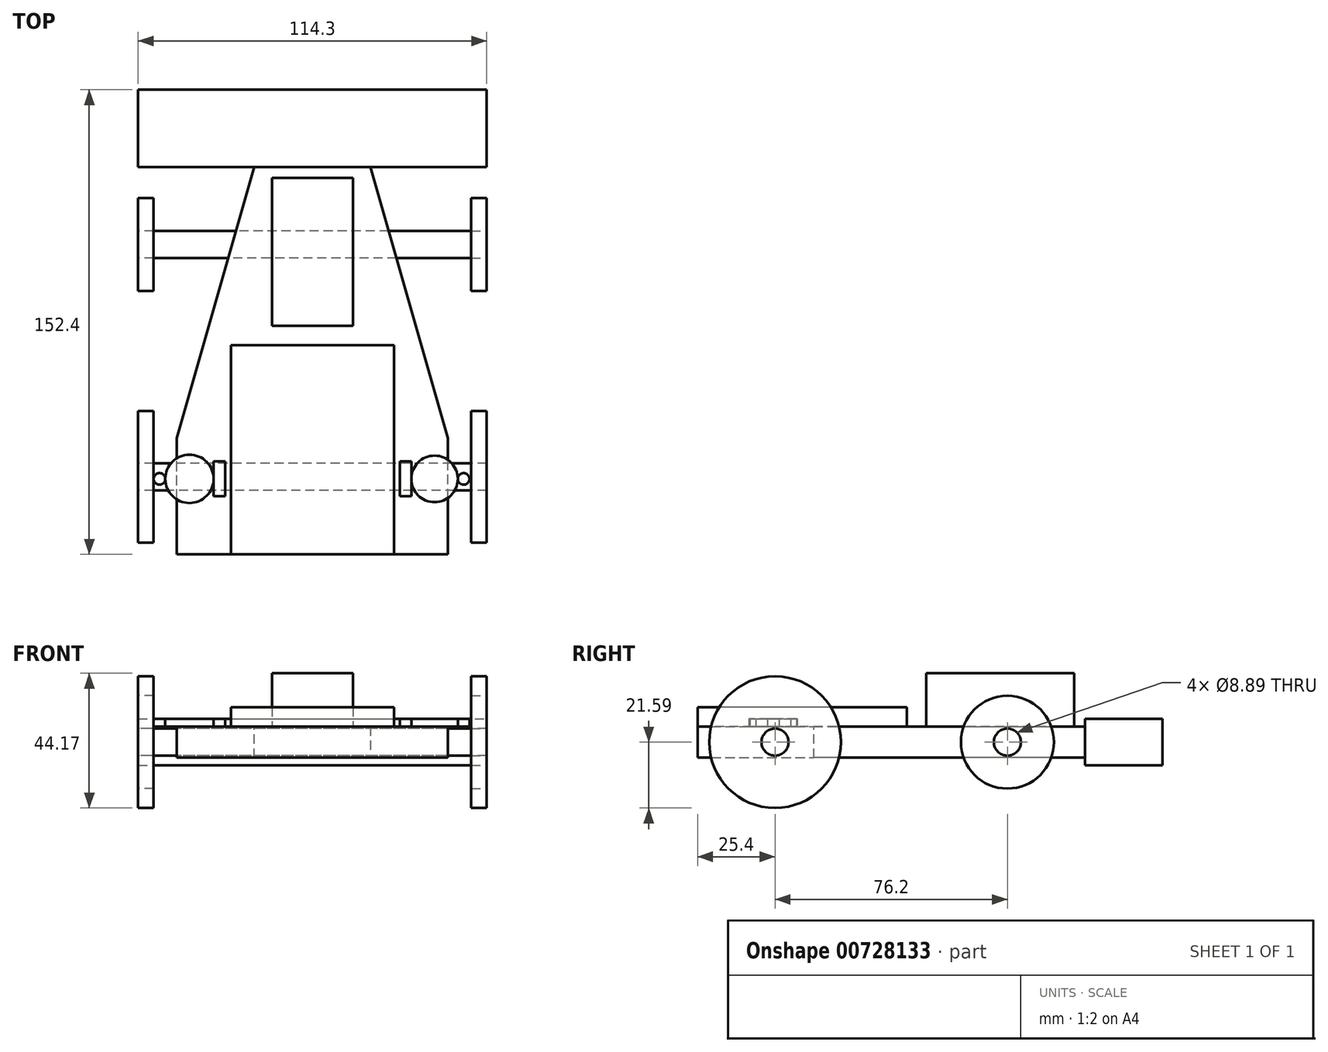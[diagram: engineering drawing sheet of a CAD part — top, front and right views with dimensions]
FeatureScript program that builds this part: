
annotation { "Feature Type Name" : "Feature", "Feature Type Description" : "" }
export const myFeature = defineFeature(function(context is Context, id is Id, definition is map)
    precondition{}
    {
        {
            var Q0;
            Q0=qCreatedBy(makeId("Front.planeOp"),FACE);
            var sketch = newSketch(context, id + "F0", { "sketchPlane" : qUnion([Q0])});
            skLineSegment(sketch, "E0.bottom", {"start": v(44.45, 5.08) * mm, "end": v(-44.45, 5.08) * mm});
            skLineSegment(sketch, "E0.top", {"start": v(44.45, -5.08) * mm, "end": v(-44.45, -5.08) * mm});
            skLineSegment(sketch, "E0.left", {"start": v(44.45, 5.08) * mm, "end": v(44.45, -5.08) * mm});
            skLineSegment(sketch, "E0.right", {"start": v(-44.45, 5.08) * mm, "end": v(-44.45, -5.08) * mm});
            skPoint(sketch, "E0.middle", {"position": v(0, 0) * mm});
            skSolve(sketch);
        }
        {
            var Q0;
            Q0=makeQuery(id+"F0.imprint","IMPRINT",FACE,{"disambiguationData":[TD([[makeQuery(id+"F0.imprint","IMPRINT",EDGE,{"derivedFrom":sQuery(id+"F0.wireOp",EDGE,"E0.bottom")}),1.0]])]});
            extrude(context, id + "F1", {"entities" : qUnion([Q0]), "endBound" : BoundingType.SYMMETRIC, "depth" : 127 * mm, "offsetDistance" : 25.4 * mm});
        }
        {
            var Q0;
            Q0=makeQuery(id+"F1.opExtrude","SWEPT_FACE",FACE,{"disambiguationData":[OSD([sQuery(id+"F0.wireOp",EDGE,"E0.bottom")])]});
            var sketch = newSketch(context, id + "F2", { "sketchPlane" : qUnion([Q0])});
            skLineSegment(sketch, "E1.bottom", {"start": v(26.7, 5.1) * mm, "end": v(-26.7, 5.1) * mm});
            skLineSegment(sketch, "E1.top", {"start": v(26.7, -63.5) * mm, "end": v(-26.7, -63.5) * mm});
            skLineSegment(sketch, "E1.left", {"start": v(26.7, 5.1) * mm, "end": v(26.7, -63.5) * mm});
            skLineSegment(sketch, "E1.right", {"start": v(-26.7, 5.1) * mm, "end": v(-26.7, -63.5) * mm});
            skPoint(sketch, "E1.middle", {"position": v(0, -29.2) * mm});
            skLineSegment(sketch, "E2.bottom", {"start": v(13.25, 59.95) * mm, "end": v(-13.25, 59.95) * mm});
            skLineSegment(sketch, "E2.top", {"start": v(13.25, 11.45) * mm, "end": v(-13.25, 11.45) * mm});
            skLineSegment(sketch, "E2.left", {"start": v(13.25, 59.95) * mm, "end": v(13.25, 11.45) * mm});
            skLineSegment(sketch, "E2.right", {"start": v(-13.25, 59.95) * mm, "end": v(-13.25, 11.45) * mm});
            skPoint(sketch, "E2.middle", {"position": v(0, 35.7) * mm});
            skSolve(sketch);
        }
        {
            var Q0;
            Q0=makeQuery(id+"F2.imprint","IMPRINT",FACE,{"disambiguationData":[TD([[makeQuery(id+"F2.imprint","IMPRINT",EDGE,{"derivedFrom":sQuery(id+"F2.wireOp",EDGE,"E1.bottom")}),1.0]])]});
            extrude(context, id + "F3", {"entities" : qUnion([Q0]), "depth" : 6.35 * mm, "offsetDistance" : 25.4 * mm});
        }
        {
            var Q0;
            Q0=qCreatedBy(makeId("Right.planeOp"),FACE);
            var sketch = newSketch(context, id + "F4", { "sketchPlane" : qUnion([Q0])});
            skCircle(sketch, "E3", {"center": v(-38.1, 0) * mm, "radius": 4.45 * mm});
            skCircle(sketch, "E4", {"center": v(38.1, 0) * mm, "radius": 4.45 * mm});
            skSolve(sketch);
        }
        {
            var Q0;
            Q0 = qSketchRegion(id + "F4", true);
            extrude(context, id + "F5", {"entities" : qUnion([Q0]), "endBound" : BoundingType.SYMMETRIC, "depth" : 114.3 * mm, "offsetDistance" : 25.4 * mm});
        }
        {
            var Q0;
            Q0=makeQuery(id+"F5.opExtrude","CAP_FACE",FACE,{"disambiguationData":[OSD([sQuery(id+"F4.wireOp",EDGE,"E3")])],"isStart":false});
            var sketch = newSketch(context, id + "F6", { "sketchPlane" : qUnion([Q0])});
            skCircle(sketch, "E5", {"center": v(-38.1, 0) * mm, "radius": 21.59 * mm});
            skCircle(sketch, "E6", {"center": v(38.1, 0) * mm, "radius": 15.24 * mm});
            skCircle(sketch, "E7", {"center": v(-38.1, 0) * mm, "radius": 4.45 * mm});
            skCircle(sketch, "E8", {"center": v(38.1, 0) * mm, "radius": 4.45 * mm});
            skSolve(sketch);
        }
        {
            var Q0;
            Q0 = qSketchRegion(id + "F6", true);
            extrude(context, id + "F7", {"entities" : qUnion([Q0]), "depth" : -5.08 * mm, "offsetDistance" : 25.4 * mm});
        }
        {
            var Q0;
            Q0=makeQuery(id+"F5.opExtrude","CAP_FACE",FACE,{"disambiguationData":[OSD([sQuery(id+"F4.wireOp",EDGE,"E4")])],"isStart":true});
            var sketch = newSketch(context, id + "F8", { "sketchPlane" : qUnion([Q0])});
            skCircle(sketch, "E9", {"center": v(-38.1, 0) * mm, "radius": 15.24 * mm});
            skCircle(sketch, "E10", {"center": v(-38.1, 0) * mm, "radius": 4.45 * mm});
            skCircle(sketch, "E11", {"center": v(38.1, 0) * mm, "radius": 21.59 * mm});
            skCircle(sketch, "E12", {"center": v(38.1, 0) * mm, "radius": 4.45 * mm});
            skSolve(sketch);
        }
        {
            var Q0;
            Q0 = qSketchRegion(id + "F8", true);
            extrude(context, id + "F9", {"entities" : qUnion([Q0]), "depth" : -5.08 * mm, "offsetDistance" : 25.4 * mm});
        }
        {
            var Q0;
            Q0=makeQuery(id+"F1.opExtrude","SWEPT_FACE",FACE,{"disambiguationData":[OSD([sQuery(id+"F0.wireOp",EDGE,"E0.bottom")])]});
            var sketch = newSketch(context, id + "F10", { "sketchPlane" : qUnion([Q0])});
            skLineSegment(sketch, "E13.bottom", {"start": v(28.6, -44.45) * mm, "end": v(32.41, -44.45) * mm});
            skLineSegment(sketch, "E13.top", {"start": v(28.6, -33.02) * mm, "end": v(32.41, -33.02) * mm});
            skLineSegment(sketch, "E13.left", {"start": v(28.6, -44.45) * mm, "end": v(28.6, -33.02) * mm});
            skLineSegment(sketch, "E13.right", {"start": v(32.41, -44.45) * mm, "end": v(32.41, -33.02) * mm});
            skLineSegment(sketch, "E14.bottom", {"start": v(-28.6, -44.45) * mm, "end": v(-32.41, -44.45) * mm});
            skLineSegment(sketch, "E14.top", {"start": v(-28.6, -33.02) * mm, "end": v(-32.41, -33.02) * mm});
            skLineSegment(sketch, "E14.left", {"start": v(-28.6, -44.45) * mm, "end": v(-28.6, -33.02) * mm});
            skLineSegment(sketch, "E14.right", {"start": v(-32.41, -44.45) * mm, "end": v(-32.41, -33.02) * mm});
            skCircle(sketch, "E15", {"center": v(-40.34, -38.73) * mm, "radius": 7.92 * mm});
            skCircle(sketch, "E16", {"center": v(40.03, -38.73) * mm, "radius": 7.62 * mm});
            skCircle(sketch, "E17", {"center": v(-50.17, -38.73) * mm, "radius": 1.9 * mm});
            skCircle(sketch, "E18", {"center": v(49.56, -38.73) * mm, "radius": 1.9 * mm});
            skSolve(sketch);
        }
        {
            var Q0;
            Q0 = qSketchRegion(id + "F10", true);
            extrude(context, id + "F11", {"entities" : qUnion([Q0]), "depth" : 2.54 * mm, "offsetDistance" : 25.4 * mm});
        }
        {
            var Q0;
            Q0=makeQuery(id+"F2.imprint","IMPRINT",FACE,{"disambiguationData":[TD([[makeQuery(id+"F2.imprint","IMPRINT",EDGE,{"derivedFrom":sQuery(id+"F2.wireOp",EDGE,"E2.bottom")}),1.0]])]});
            extrude(context, id + "F12", {"entities" : qUnion([Q0]), "depth" : 17.5 * mm, "offsetDistance" : 25.4 * mm});
        }
        {
            var Q0;
            Q0=makeQuery(id+"F1.opExtrude","CAP_EDGE",EDGE,{"disambiguationData":[OSD([sQuery(id+"F0.wireOp",EDGE,"E0.left")])],"isStart":true});
            var Q1;
            Q1=makeQuery(id+"F1.opExtrude","CAP_EDGE",EDGE,{"disambiguationData":[OSD([sQuery(id+"F0.wireOp",EDGE,"E0.right")])],"isStart":true});
            chamfer(context, id + "F13", {"entities" : qUnion([Q0, Q1]), "chamferType" : ChamferType.TWO_OFFSETS, "width1" : 25.4 * mm, "oppositeDirection" : false, "width2" : 88.9 * mm, "tangentPropagation" : true});
        }
        {
            var Q0;
            Q0=makeQuery(id+"F1.opExtrude","CAP_FACE",FACE,{"disambiguationData":[OSD([sQuery(id+"F0.wireOp",EDGE,"E0.bottom"),sQuery(id+"F0.wireOp",EDGE,"E0.top"),sQuery(id+"F0.wireOp",EDGE,"E0.left"),sQuery(id+"F0.wireOp",EDGE,"E0.right")])],"isStart":true});
            var sketch = newSketch(context, id + "F14", { "sketchPlane" : qUnion([Q0])});
            skLineSegment(sketch, "E19.bottom", {"start": v(57.15, 7.62) * mm, "end": v(-57.15, 7.62) * mm});
            skLineSegment(sketch, "E19.top", {"start": v(57.15, -7.62) * mm, "end": v(-57.15, -7.62) * mm});
            skLineSegment(sketch, "E19.left", {"start": v(57.15, 7.62) * mm, "end": v(57.15, -7.62) * mm});
            skLineSegment(sketch, "E19.right", {"start": v(-57.15, 7.62) * mm, "end": v(-57.15, -7.62) * mm});
            skPoint(sketch, "E19.middle", {"position": v(0, 0) * mm});
            skSolve(sketch);
        }
        {
            var Q0;
            Q0 = qSketchRegion(id + "F14", true);
            extrude(context, id + "F15", {"entities" : qUnion([Q0]), "operationType" : NewBodyOperationType.ADD, "depth" : 25.4 * mm, "offsetDistance" : 25.4 * mm});
        }
        {
            var Q0;
            Q0=makeQuery(id+"F15.opExtrude","SWEPT_FACE",FACE,{"disambiguationData":[OSD([sQuery(id+"F14.wireOp",EDGE,"E19.bottom")])]});
            var sketch = newSketch(context, id + "F16", { "sketchPlane" : qUnion([Q0])});
            skLineSegment(sketch, "E20", {"start": v(-16.5, 63.5) * mm, "end": v(-57.15, 74.93) * mm});
            skLineSegment(sketch, "E21", {"start": v(-57.15, 77.47) * mm, "end": v(-7.37, 63.5) * mm});
            skLineSegment(sketch, "E22", {"start": v(7.37, 63.5) * mm, "end": v(57.15, 77.47) * mm});
            skLineSegment(sketch, "E23", {"start": v(16.5, 63.5) * mm, "end": v(57.15, 74.93) * mm});
            skSolve(sketch);
        }
        {
            var Q0;
            {var subQ0=sQuery(id+"F16.wireOp",EDGE,"E20");Q0=makeQuery(id+"F16.imprint","IMPRINT",FACE,{"disambiguationData":[TD([[makeQuery(id+"F16.imprint","IMPRINT",EDGE,{"derivedFrom":subQ0}),-1.0]])]});}
            var Q1;
            {var subQ0=sQuery(id+"F16.wireOp",EDGE,"E22");Q1=makeQuery(id+"F16.imprint","IMPRINT",FACE,{"disambiguationData":[TD([[makeQuery(id+"F16.imprint","IMPRINT",EDGE,{"derivedFrom":subQ0}),-1.0]])]});}
            extrude(context, id + "F17", {"entities" : qUnion([Q0, Q1]), "operationType" : NewBodyOperationType.ADD, "depth" : -15.24 * mm, "offsetDistance" : 25.4 * mm});
        }
    });
